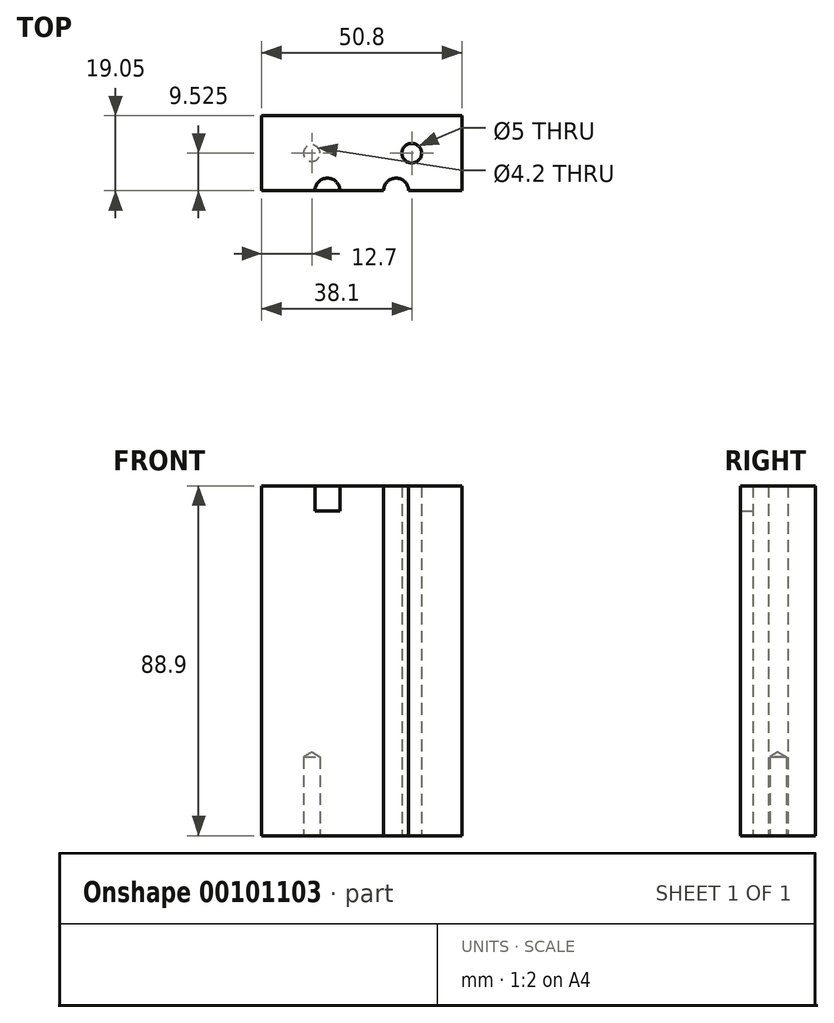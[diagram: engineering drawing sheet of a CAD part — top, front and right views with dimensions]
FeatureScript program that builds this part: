
annotation { "Feature Type Name" : "Feature", "Feature Type Description" : "" }
export const myFeature = defineFeature(function(context is Context, id is Id, definition is map)
    precondition{}
    {
        {
            var Q0;
            Q0=qCreatedBy(makeId("Top.planeOp"),FACE);
            var sketch = newSketch(context, id + "F0", { "sketchPlane" : qUnion([Q0])});
            skLineSegment(sketch, "E0.bottom", {"start": v(25.4, 0) * mm, "end": v(0, 0) * mm});
            skLineSegment(sketch, "E0.top", {"start": v(25.4, 19.05) * mm, "end": v(0, 19.05) * mm});
            skLineSegment(sketch, "E0.left", {"start": v(25.4, 0) * mm, "end": v(25.4, 19.05) * mm, "construction": true});
            skLineSegment(sketch, "E0.right", {"start": v(0, 0) * mm, "end": v(0, 19.05) * mm});
            skLineSegment(sketch, "E1.MirrorCS", {"start": v(25.4, 19.05) * mm, "end": v(50.8, 19.05) * mm});
            skLineSegment(sketch, "E2.MirrorCS", {"start": v(50.8, 0) * mm, "end": v(50.8, 19.05) * mm});
            skLineSegment(sketch, "E3.MirrorCS", {"start": v(25.4, 0) * mm, "end": v(50.8, 0) * mm});
            skLineSegment(sketch, "E4", {"start": v(25.4, 0) * mm, "end": v(16.67, 0) * mm});
            skLineSegment(sketch, "E5", {"start": v(16.67, 0) * mm, "end": v(34.13, 0) * mm});
            skArc(sketch, "E6", {"start": v(19.84, 0) * mm, "mid": v(16.67, 3.18) * mm, "end": v(13.5, 0) * mm});
            skArc(sketch, "E7", {"start": v(37.3, 0) * mm, "mid": v(34.13, 3.17) * mm, "end": v(30.96, 0) * mm});
            skPoint(sketch, "E8.endSnap0", {"position": v(12.7, 19.05) * mm});
            skCircle(sketch, "E9", {"center": v(12.7, 9.53) * mm, "radius": 2.5 * mm});
            skCircle(sketch, "E10.MirrorC", {"center": v(38.1, 9.53) * mm, "radius": 2.5 * mm});
            skSolve(sketch);
        }
        {
            var Q0;
            Q0=makeQuery(id+"F0.imprint","IMPRINT",FACE,{"disambiguationData":[TD([[makeQuery(id+"F0.imprint","IMPRINT",EDGE,{"derivedFrom":sQuery(id+"F0.wireOp",EDGE,"E0.top")}),1.0]])]});
            var Q1;
            Q1=makeQuery(id+"F0.imprint","IMPRINT",FACE,{"disambiguationData":[TD([[makeQuery(id+"F0.imprint","IMPRINT",EDGE,{"derivedFrom":sQuery(id+"F0.wireOp",EDGE,"E9")}),1.0]])]});
            var Q2;
            Q2=makeQuery(id+"F0.imprint","IMPRINT",FACE,{"disambiguationData":[TD([[makeQuery(id+"F0.imprint","IMPRINT",EDGE,{"derivedFrom":sQuery(id+"F0.wireOp",EDGE,"E10.MirrorC")}),-1.0]])]});
            extrude(context, id + "F1", {"entities" : qUnion([Q0, Q1, Q2]), "depth" : 88.9 * mm});
        }
        {
            var Q0;
            {var subQ0=sQuery(id+"F0.wireOp",EDGE,"E5");var subQ1=sQuery(id+"F0.wireOp",EDGE,"E0.bottom");var subQ2=makeQuery(id+"F0.imprint","INTERSECT",VERTEX,{"derivedFrom":[subQ1,subQ0]});Q0=makeQuery(id+"F0.imprint","IMPRINT",FACE,{"disambiguationData":[TD([[makeQuery(id+"F0.imprint","IMPRINT",EDGE,{"disambiguationData":[TD([[subQ2,-1.0]])],"derivedFrom":subQ1}),-1.0]])]});}
            var Q1;
            {var subQ0=sQuery(id+"F0.wireOp",EDGE,"E5");var subQ1=sQuery(id+"F0.wireOp",EDGE,"E3.MirrorCS");var subQ2=makeQuery(id+"F0.imprint","INTERSECT",VERTEX,{"derivedFrom":[subQ1,subQ0]});Q1=makeQuery(id+"F0.imprint","IMPRINT",FACE,{"disambiguationData":[TD([[makeQuery(id+"F0.imprint","IMPRINT",EDGE,{"disambiguationData":[TD([[subQ2,-1.0]])],"derivedFrom":subQ1}),1.0]])]});}
            extrude(context, id + "F2", {"entities" : qUnion([Q0, Q1]), "operationType" : NewBodyOperationType.ADD, "depth" : 82.55 * mm});
        }
        {
            var Q0;
            Q0=sQuery(id+"F0.wireOp",VERTEX,"E9.center");
            var Q1;
            Q1=sQuery(id+"F0.wireOp",VERTEX,"E10.MirrorC.center");
            var Q2;
            Q2=makeQuery(id+"F1.opExtrude","SWEPT_BODY",BODY,{"disambiguationData":[OSD([sQuery(id+"F0.wireOp",EDGE,"E0.bottom"),sQuery(id+"F0.wireOp",EDGE,"E0.top"),sQuery(id+"F0.wireOp",EDGE,"E0.right"),sQuery(id+"F0.wireOp",EDGE,"E1.MirrorCS"),sQuery(id+"F0.wireOp",EDGE,"E2.MirrorCS"),sQuery(id+"F0.wireOp",EDGE,"E3.MirrorCS"),sQuery(id+"F0.wireOp",EDGE,"E5"),sQuery(id+"F0.wireOp",EDGE,"E6"),sQuery(id+"F0.wireOp",EDGE,"E7")])]});
            hole(context, id + "F3", {"style" : HoleStyle.SIMPLE, "endStyle" : HoleEndStyle.BLIND, "oppositeDirection" : true, "standardTappedOrClearance" : lookupTablePath({ "standard" : "ISO", "engagement" : "75%", "pitch" : "0.8 mm", "size" : "M5", "type" : "Tapped" }), "standardBlindInLast" : lookupTablePath({ "standard" : "ISO", "engagement" : "75%", "pitch" : "0.8 mm", "size" : "M5", "type" : "Tapped" }), "holeDiameter" : 4.2 * mm, "holeDepth" : 20 * mm, "locations" : qUnion([Q0, Q1]), "scope" : qUnion([Q2]), "majorDiameter" : 5 * mm});
        }
    });
